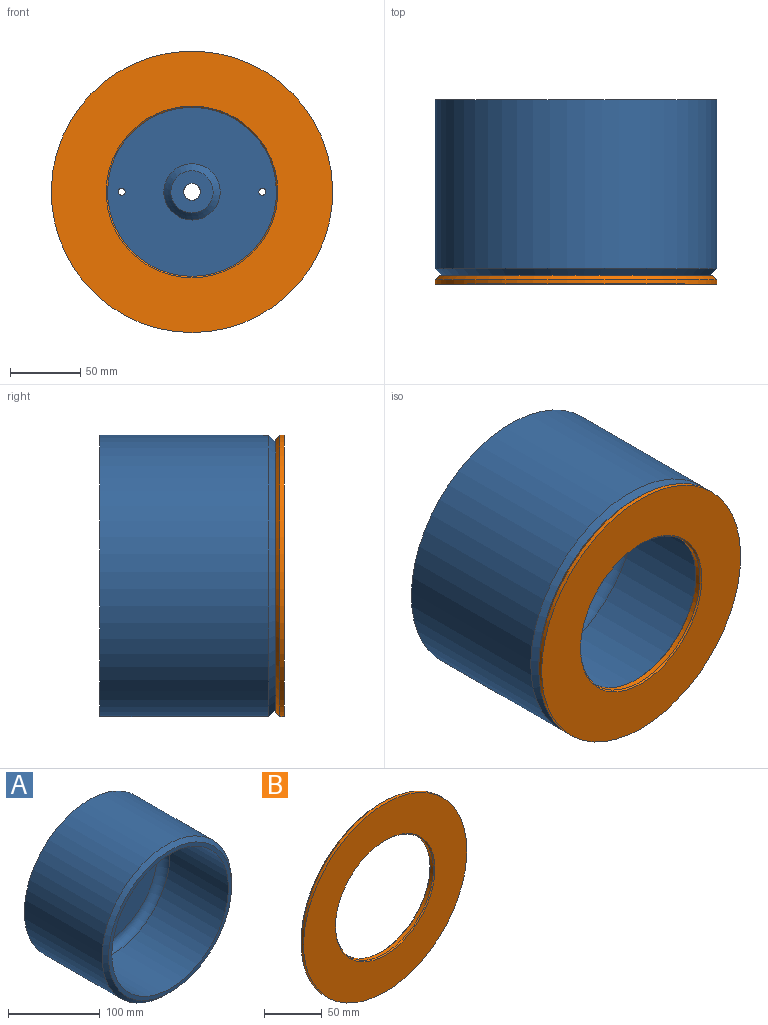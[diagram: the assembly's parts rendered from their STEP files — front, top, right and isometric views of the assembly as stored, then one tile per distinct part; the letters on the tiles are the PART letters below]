
ASSEMBLY  parts=2 mates=1
PART A: 12 faces, bbox 200x125x200 mm
  f0: cylinder r=100mm len=200mm, axis (0,1,0), area 75398.2mm2, adj f2,f5
  f1: plane 190x190mm, normal (0,-1,0), area 2906mm2, adj f3,f5
  f2: plane 200x200mm, normal (0,1,0), area 31263.6mm2, adj f0,f9,f10,f11
  f3: cylinder r=90mm len=180mm, axis (0,-1,0), area 50893.8mm2, adj f1,f6
  f4: plane 160x160mm, normal (0,-1,0), area 18810.3mm2, adj f6,f8,f10,f11
  f5: cone r=95mm half-angle=45deg, axis (0,1,0), area 4331.8mm2, adj f0,f1
  f6: torus R=80mm, axis (0,-1,0), area 8524mm2, adj f3,f4
  f7: plane 30x30mm, normal (0,-1,0), area 593.8mm2, adj f8,f9
  f8: cone r=15mm half-angle=45deg, axis (0,1,0), area 777.5mm2, adj f4,f7
  f9: cylinder r=6mm len=30mm, axis (0,1,0), area 1131mm2, adj f2,f7
  f10: cylinder r=2.5mm len=25mm, axis (0,1,0), area 392.7mm2, adj f2,f4
  f11: cylinder r=2.5mm len=25mm, axis (0,1,0), area 392.7mm2, adj f2,f4
PART B: 7 faces, bbox 200x6x200 mm
  f0: cylinder r=60mm len=120mm, axis (0,1,0), area 1508mm2, adj f4,f5
  f1: cylinder r=100mm len=200mm, axis (0,1,0), area 1885mm2, adj f2,f6
  f2: plane 200x200mm, normal (0,-1,0), area 19726.1mm2, adj f1,f5
  f3: plane 194x194mm, normal (0,1,0), area 17869.4mm2, adj f4,f6
  f4: cone r=61mm half-angle=45deg, axis (0,1,0), area 537.6mm2, adj f0,f3
  f5: cone r=60mm half-angle=45deg, axis (0,-1,0), area 537.6mm2, adj f0,f2
  f6: cone r=100mm half-angle=45deg, axis (0,-1,0), area 2625.7mm2, adj f1,f3
PLACE A t=(-114.76,8.13,17.84)mm
PLACE B t=(-114.76,-116.87,17.84)mm
MATE fastened B.f1 <-> A.f3  axis (0,1,0) through (-114.76,-116.87,17.84)mm
